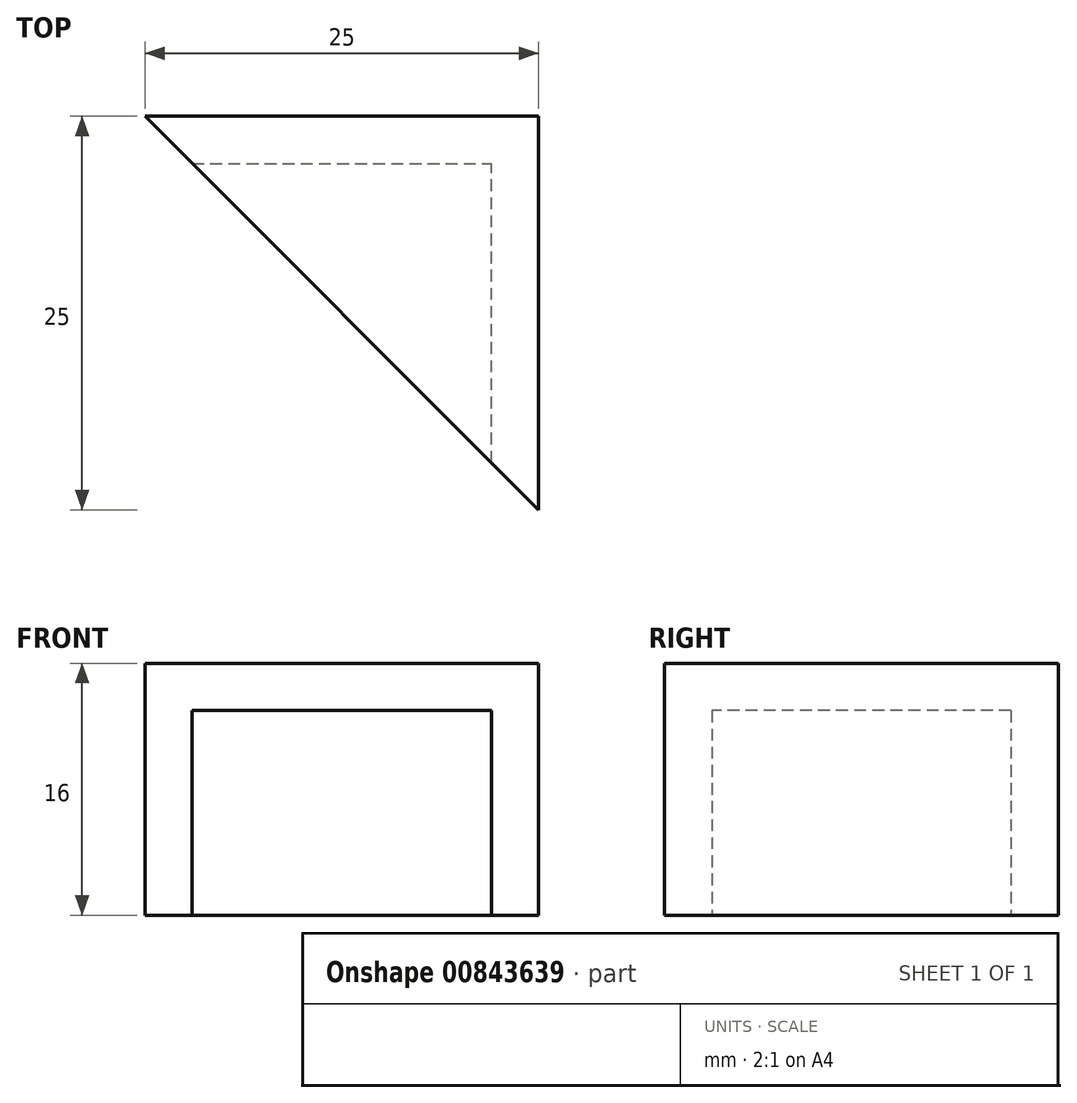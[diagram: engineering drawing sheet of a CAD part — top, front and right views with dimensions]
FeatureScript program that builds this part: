
annotation { "Feature Type Name" : "Feature", "Feature Type Description" : "" }
export const myFeature = defineFeature(function(context is Context, id is Id, definition is map)
    precondition{}
    {
        {
            var Q0;
            Q0=qCreatedBy(makeId("Top.planeOp"),FACE);
            var sketch = newSketch(context, id + "F0", { "sketchPlane" : qUnion([Q0])});
            skLineSegment(sketch, "E0.0", {"start": v(0, 25) * mm, "end": v(25, 25) * mm});
            skLineSegment(sketch, "E0.1", {"start": v(0, 0) * mm, "end": v(0, 25) * mm});
            skLineSegment(sketch, "E0.2", {"start": v(0, 0) * mm, "end": v(25, 0) * mm});
            skLineSegment(sketch, "E0.3", {"start": v(25, 0) * mm, "end": v(25, 25) * mm});
            skSolve(sketch);
        }
        {
            var Q0;
            Q0=makeQuery(id+"F0.imprint","IMPRINT",FACE,{"disambiguationData":[TD([[makeQuery(id+"F0.imprint","IMPRINT",EDGE,{"derivedFrom":sQuery(id+"F0.wireOp",EDGE,"E0.0")}),-1.0]])]});
            extrude(context, id + "F1", {"entities" : qUnion([Q0]), "depth" : 16 * mm, "offsetDistance" : 25 * mm});
        }
        {
            var Q0;
            Q0=makeQuery(id+"F1.opExtrude","CAP_FACE",FACE,{"disambiguationData":[OSD([sQuery(id+"F0.wireOp",EDGE,"E0.0"),sQuery(id+"F0.wireOp",EDGE,"E0.1"),sQuery(id+"F0.wireOp",EDGE,"E0.2"),sQuery(id+"F0.wireOp",EDGE,"E0.3")])],"isStart":true});
            shell(context, id + "F2", {"entities" : qUnion([Q0]), "thickness" : 3 * mm});
        }
        {
            var Q0;
            Q0=makeQuery(id+"F1.opExtrude","CAP_FACE",FACE,{"disambiguationData":[OSD([sQuery(id+"F0.wireOp",EDGE,"E0.0"),sQuery(id+"F0.wireOp",EDGE,"E0.1"),sQuery(id+"F0.wireOp",EDGE,"E0.2"),sQuery(id+"F0.wireOp",EDGE,"E0.3")])],"isStart":false});
            var sketch = newSketch(context, id + "F3", { "sketchPlane" : qUnion([Q0])});
            skLineSegment(sketch, "E1", {"start": v(25, 25) * mm, "end": v(0, 0) * mm});
            skLineSegment(sketch, "E2", {"start": v(0, 25) * mm, "end": v(25, 0) * mm});
            skCircle(sketch, "E3", {"center": v(12.5, 12.5) * mm, "radius": 6.5 * mm});
            skSolve(sketch);
        }
        {
            var Q0;
            {var subQ0=sQuery(id+"F3.wireOp",EDGE,"E3");var subQ1=sQuery(id+"F3.wireOp",EDGE,"E1");var subQ2=makeQuery(id+"F3.imprint","INTERSECT",VERTEX,{"disambiguationData":[OD(0.0)],"derivedFrom":[subQ1,subQ0]});Q0=makeQuery(id+"F3.imprint","IMPRINT",FACE,{"disambiguationData":[TD([[makeQuery(id+"F3.imprint","IMPRINT",EDGE,{"disambiguationData":[TD([[subQ2,-1.0]])],"derivedFrom":subQ1}),-1.0]])]});}
            var Q1;
            {var subQ0=sQuery(id+"F3.wireOp",EDGE,"E3");var subQ1=sQuery(id+"F3.wireOp",EDGE,"E1");var subQ2=makeQuery(id+"F3.imprint","INTERSECT",VERTEX,{"disambiguationData":[OD(0.0)],"derivedFrom":[subQ1,subQ0]});Q1=makeQuery(id+"F3.imprint","IMPRINT",FACE,{"disambiguationData":[TD([[makeQuery(id+"F3.imprint","IMPRINT",EDGE,{"disambiguationData":[TD([[subQ2,-1.0]])],"derivedFrom":subQ1}),1.0]])]});}
            var Q2;
            {var subQ0=sQuery(id+"F3.wireOp",EDGE,"E2");var subQ1=sQuery(id+"F3.wireOp",EDGE,"E1");var subQ2=makeQuery(id+"F3.imprint","INTERSECT",VERTEX,{"derivedFrom":[subQ1,subQ0]});Q2=makeQuery(id+"F3.imprint","IMPRINT",FACE,{"disambiguationData":[TD([[makeQuery(id+"F3.imprint","IMPRINT",EDGE,{"disambiguationData":[TD([[subQ2,-1.0]])],"derivedFrom":subQ1}),1.0]])]});}
            var Q3;
            {var subQ0=sQuery(id+"F3.wireOp",EDGE,"E2");var subQ1=sQuery(id+"F3.wireOp",EDGE,"E1");var subQ2=makeQuery(id+"F3.imprint","INTERSECT",VERTEX,{"derivedFrom":[subQ1,subQ0]});Q3=makeQuery(id+"F3.imprint","IMPRINT",FACE,{"disambiguationData":[TD([[makeQuery(id+"F3.imprint","IMPRINT",EDGE,{"disambiguationData":[TD([[subQ2,-1.0]])],"derivedFrom":subQ1}),-1.0]])]});}
            extrude(context, id + "F4", {"entities" : qUnion([Q0, Q1, Q2, Q3]), "operationType" : NewBodyOperationType.REMOVE, "oppositeDirection" : true, "depth" : 25 * mm, "offsetDistance" : 25 * mm});
        }
    });
